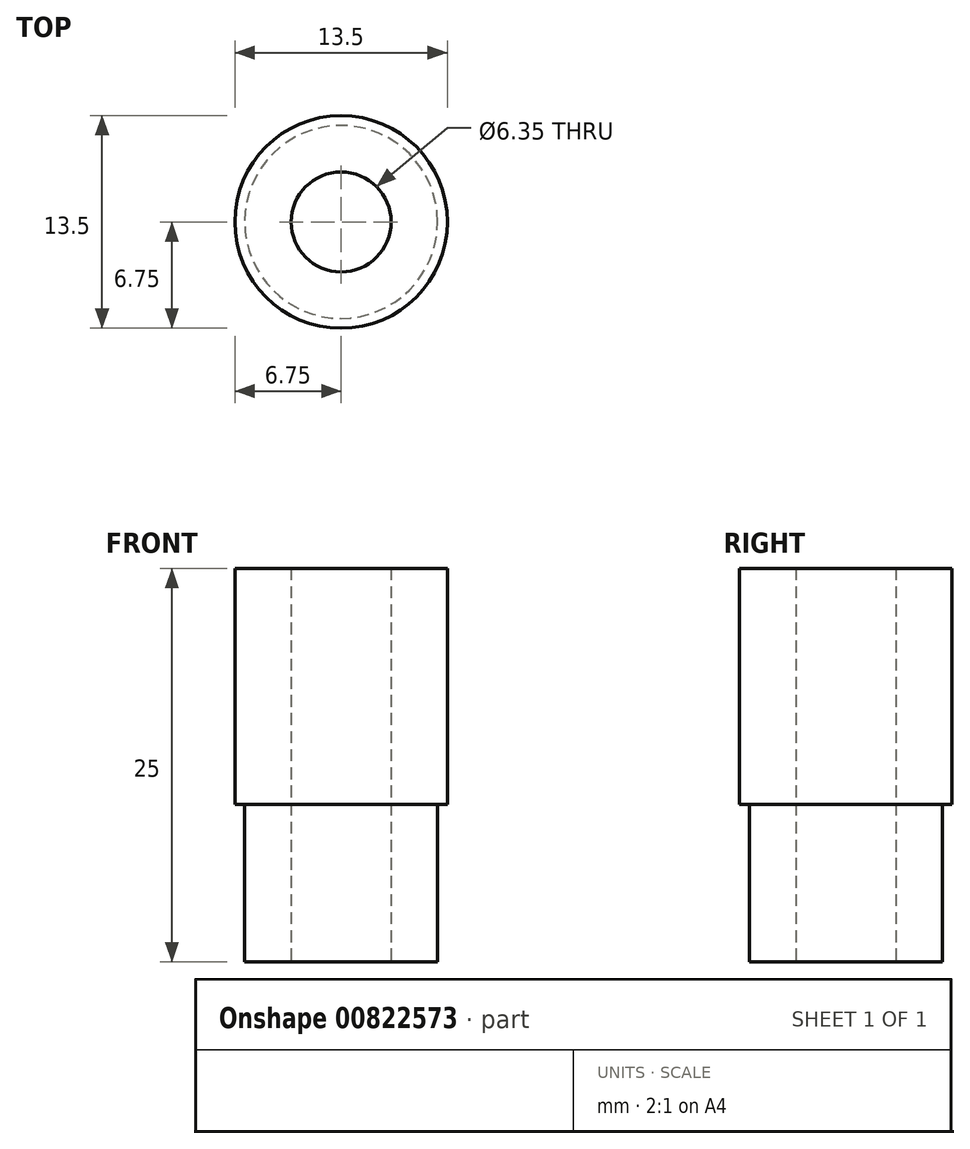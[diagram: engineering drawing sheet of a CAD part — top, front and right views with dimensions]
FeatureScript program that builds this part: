
annotation { "Feature Type Name" : "Feature", "Feature Type Description" : "" }
export const myFeature = defineFeature(function(context is Context, id is Id, definition is map)
    precondition{}
    {
        {
            var Q0;
            Q0=qCreatedBy(makeId("Top.planeOp"),FACE);
            var sketch = newSketch(context, id + "F0", { "sketchPlane" : qUnion([Q0])});
            skCircle(sketch, "E0", {"center": v(0, 0) * mm, "radius": 6.75 * mm});
            skCircle(sketch, "E1", {"center": v(0, 0) * mm, "radius": 1.98 * mm});
            skCircle(sketch, "E2", {"center": v(0, 0) * mm, "radius": 2.38 * mm});
            skCircle(sketch, "E3", {"center": v(0, 0) * mm, "radius": 3.17 * mm});
            skCircle(sketch, "E4", {"center": v(0, 0) * mm, "radius": 6.12 * mm});
            skSolve(sketch);
        }
        {
            var Q0;
            Q0=makeQuery(id+"F0.imprint","IMPRINT",FACE,{"disambiguationData":[TD([[makeQuery(id+"F0.imprint","IMPRINT",EDGE,{"derivedFrom":sQuery(id+"F0.wireOp",EDGE,"E3")}),-1.0]])]});
            var Q1;
            Q1=makeQuery(id+"F0.imprint","IMPRINT",FACE,{"disambiguationData":[TD([[makeQuery(id+"F0.imprint","IMPRINT",EDGE,{"derivedFrom":sQuery(id+"F0.wireOp",EDGE,"E0")}),1.0]])]});
            extrude(context, id + "F1", {"entities" : qUnion([Q0, Q1]), "depth" : 15 * mm, "offsetDistance" : 25 * mm});
        }
        {
            var Q0;
            Q0=makeQuery(id+"F0.imprint","IMPRINT",FACE,{"disambiguationData":[TD([[makeQuery(id+"F0.imprint","IMPRINT",EDGE,{"derivedFrom":sQuery(id+"F0.wireOp",EDGE,"E3")}),-1.0]])]});
            extrude(context, id + "F2", {"entities" : qUnion([Q0]), "operationType" : NewBodyOperationType.ADD, "oppositeDirection" : true, "depth" : 10 * mm, "offsetDistance" : 25 * mm});
        }
    });
